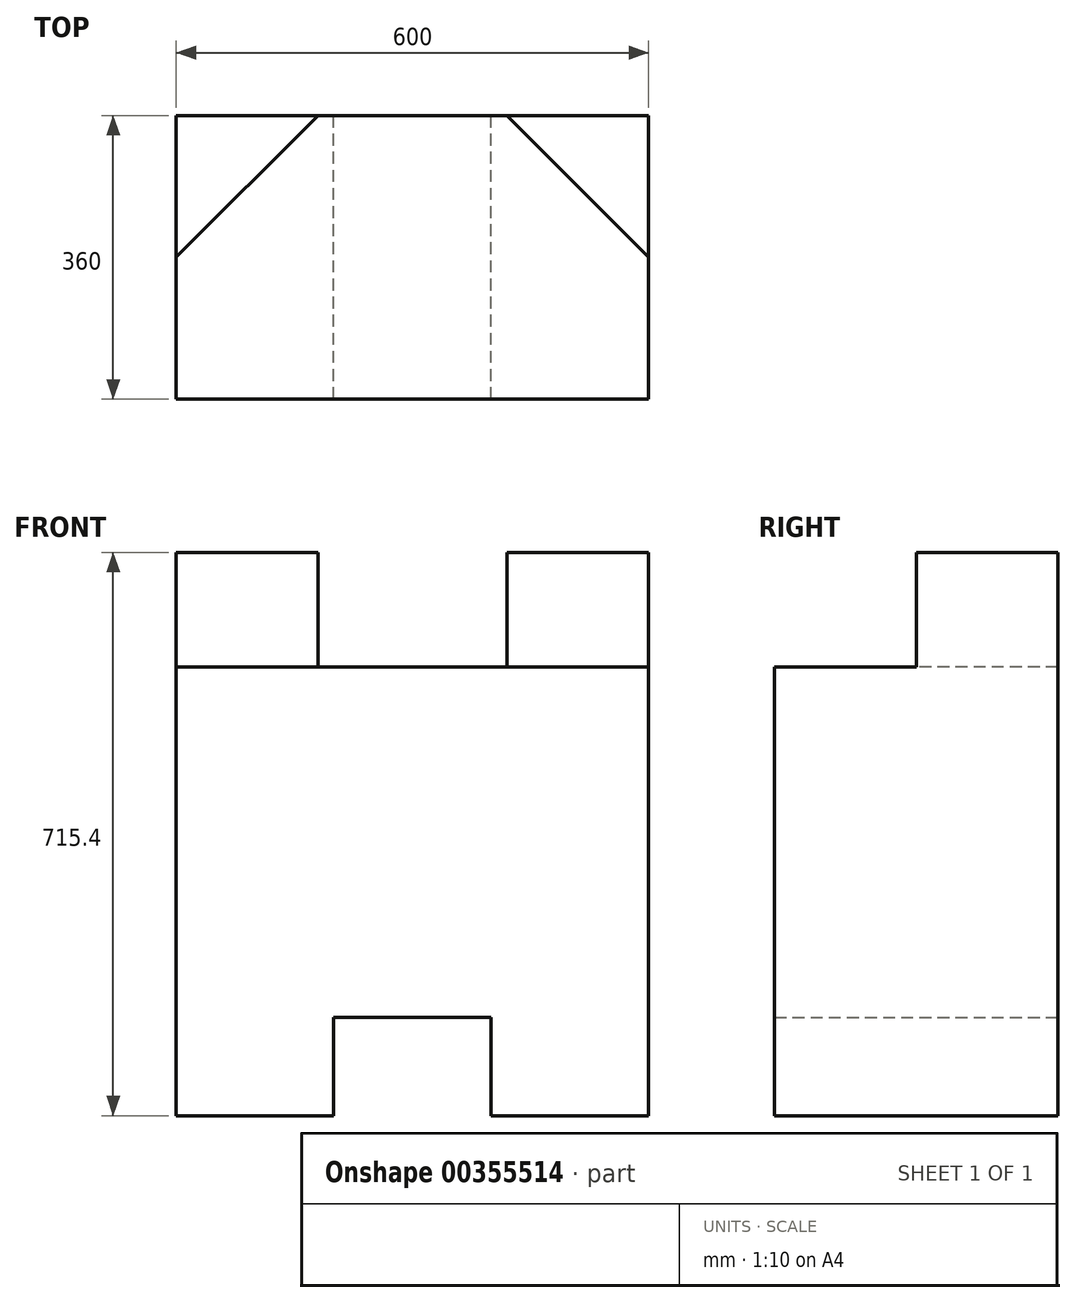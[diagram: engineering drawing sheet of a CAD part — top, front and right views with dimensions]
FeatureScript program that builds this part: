
annotation { "Feature Type Name" : "Feature", "Feature Type Description" : "" }
export const myFeature = defineFeature(function(context is Context, id is Id, definition is map)
    precondition{}
    {
        {
            var Q0;
            Q0=qCreatedBy(makeId("Front.planeOp"),FACE);
            var sketch = newSketch(context, id + "F0", { "sketchPlane" : qUnion([Q0])});
            skLineSegment(sketch, "E0.bottom", {"start": v(260.32, 285) * mm, "end": v(-339.68, 285) * mm});
            skLineSegment(sketch, "E0.top", {"start": v(260.32, -285) * mm, "end": v(60.32, -285) * mm});
            skLineSegment(sketch, "E0.left", {"start": v(260.32, 285) * mm, "end": v(260.32, -285) * mm});
            skLineSegment(sketch, "E0.right", {"start": v(-339.68, 285) * mm, "end": v(-339.68, -285) * mm});
            skPoint(sketch, "E0.middle", {"position": v(-39.68, 0) * mm});
            skLineSegment(sketch, "E1.top", {"start": v(60.32, -160) * mm, "end": v(-139.68, -160) * mm});
            skLineSegment(sketch, "E1.left", {"start": v(60.32, -285) * mm, "end": v(60.32, -160) * mm});
            skLineSegment(sketch, "E1.right", {"start": v(-139.68, -285) * mm, "end": v(-139.68, -160) * mm});
            skPoint(sketch, "E1.middle", {"position": v(-39.68, -285) * mm});
            skPoint(sketch, "E1.bottom.start.orphan", {"position": v(60.32, -410) * mm});
            skPoint(sketch, "E2.orphan", {"position": v(-139.68, -410) * mm});
            skLineSegment(sketch, "E3.trimOffspring", {"start": v(-139.68, -285) * mm, "end": v(-339.68, -285) * mm});
            skSolve(sketch);
        }
        {
            var Q0;
            Q0 = qSketchRegion(id + "F0", true);
            extrude(context, id + "F1", {"entities" : qUnion([Q0]), "depth" : 360 * mm});
        }
        {
            var Q0;
            Q0=makeQuery(id+"F1.opExtrude","SWEPT_FACE",FACE,{"disambiguationData":[OSD([sQuery(id+"F0.wireOp",EDGE,"E0.bottom")])]});
            var sketch = newSketch(context, id + "F2", { "sketchPlane" : qUnion([Q0])});
            skLineSegment(sketch, "E4", {"start": v(-339.68, 0) * mm, "end": v(-339.68, -180) * mm});
            skLineSegment(sketch, "E5", {"start": v(-339.68, -180) * mm, "end": v(-159.68, 0) * mm});
            skLineSegment(sketch, "E6", {"start": v(-159.68, 0) * mm, "end": v(-339.68, 0) * mm});
            skLineSegment(sketch, "E7", {"start": v(80.32, 0) * mm, "end": v(260.32, -180) * mm});
            skLineSegment(sketch, "E8", {"start": v(260.32, -180) * mm, "end": v(260.32, 0) * mm});
            skLineSegment(sketch, "E9", {"start": v(260.32, 0) * mm, "end": v(80.32, 0) * mm});
            skSolve(sketch);
        }
        {
            var Q0;
            Q0 = qSketchRegion(id + "F2", true);
            extrude(context, id + "F3", {"entities" : qUnion([Q0]), "operationType" : NewBodyOperationType.ADD, "depth" : 25.4 * mm});
        }
        {
            var Q0;
            Q0=makeQuery(id+"F3.opExtrude","CAP_FACE",FACE,{"disambiguationData":[OSD([sQuery(id+"F2.wireOp",EDGE,"E4"),sQuery(id+"F2.wireOp",EDGE,"E5"),sQuery(id+"F2.wireOp",EDGE,"E6")])],"isStart":false});
            var Q1;
            Q1=makeQuery(id+"F3.opExtrude","CAP_FACE",FACE,{"disambiguationData":[OSD([sQuery(id+"F2.wireOp",EDGE,"E7"),sQuery(id+"F2.wireOp",EDGE,"E8"),sQuery(id+"F2.wireOp",EDGE,"E9")])],"isStart":false});
            extrude(context, id + "F4", {"entities" : qUnion([Q0, Q1]), "operationType" : NewBodyOperationType.ADD, "depth" : 120 * mm});
        }
    });
